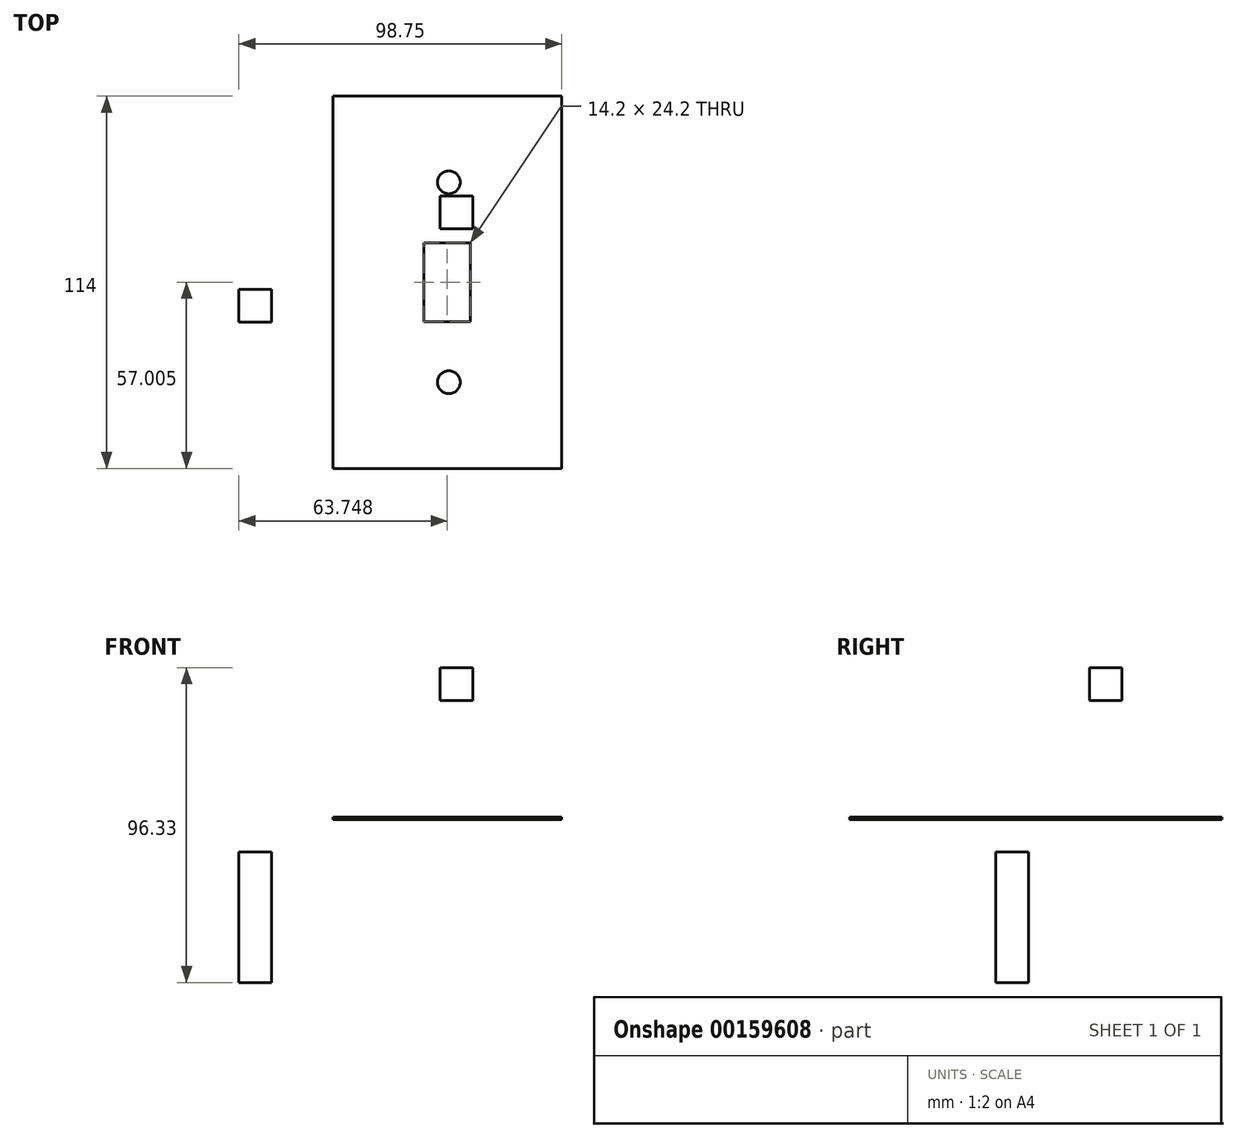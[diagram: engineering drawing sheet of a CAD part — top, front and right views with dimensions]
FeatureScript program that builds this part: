
annotation { "Feature Type Name" : "Feature", "Feature Type Description" : "" }
export const myFeature = defineFeature(function(context is Context, id is Id, definition is map)
    precondition{}
    {
        {
            assignVariable(context, id + "F0", {"name" : "W", "anyValue" : 1});
        }
        {
            var Q0;
            Q0=qCreatedBy(makeId("Top.planeOp"),FACE);
            var sketch = newSketch(context, id + "F1", { "sketchPlane" : qUnion([Q0])});
            skLineSegment(sketch, "E0.bottom", {"start": v(-32.81, 59.22) * mm, "end": v(37.19, 59.22) * mm});
            skLineSegment(sketch, "E0.top", {"start": v(-32.81, -54.78) * mm, "end": v(37.19, -54.78) * mm});
            skLineSegment(sketch, "E0.left", {"start": v(-32.81, 59.22) * mm, "end": v(-32.81, -54.78) * mm});
            skLineSegment(sketch, "E0.right", {"start": v(37.19, 59.22) * mm, "end": v(37.19, -54.78) * mm});
            skLineSegment(sketch, "E1.bottom", {"start": v(-4.91, 14.32) * mm, "end": v(9.29, 14.32) * mm});
            skLineSegment(sketch, "E1.top", {"start": v(-4.91, -9.88) * mm, "end": v(9.29, -9.88) * mm});
            skLineSegment(sketch, "E1.left", {"start": v(-4.91, 14.32) * mm, "end": v(-4.91, -9.88) * mm});
            skLineSegment(sketch, "E1.right", {"start": v(9.29, 14.32) * mm, "end": v(9.29, -9.88) * mm});
            skCircle(sketch, "E2", {"center": v(2.69, 32.82) * mm, "radius": 3.5 * mm});
            skCircle(sketch, "E3", {"center": v(2.69, -28.38) * mm, "radius": 3.5 * mm});
            skSolve(sketch);
        }
        {
            var Q0;
            Q0=makeQuery(id+"F1.imprint","IMPRINT",FACE,{"disambiguationData":[TD([[makeQuery(id+"F1.imprint","IMPRINT",EDGE,{"derivedFrom":sQuery(id+"F1.wireOp",EDGE,"E0.bottom")}),-1.0]])]});
            extrude(context, id + "F2", {"entities" : qUnion([Q0]), "depth" : (getVariable(context, 'W') * .671) * mm});
        }
        {
            var Q0;
            Q0=makeQuery(id+"F2.opExtrude","CAP_EDGE",EDGE,{"disambiguationData":[OSD([sQuery(id+"F1.wireOp",EDGE,"E2")])],"isStart":false});
            var Q1;
            Q1=makeQuery(id+"F2.opExtrude","CAP_EDGE",EDGE,{"disambiguationData":[OSD([sQuery(id+"F1.wireOp",EDGE,"E3")])],"isStart":false});
            fillet(context, id + "F3", {"entities" : qUnion([Q0, Q1]), "radius" : 1 * mm, "tangentPropagation" : true, "allowEdgeOverflow" : false});
        }
        {
            var Q0;
            Q0=qCreatedBy(makeId("Front.planeOp"),FACE);
            var sketch = newSketch(context, id + "F4", { "sketchPlane" : qUnion([Q0])});
            skLineSegment(sketch, "E4.bottom", {"start": v(-61.56, -9.89) * mm, "end": v(-51.56, -9.89) * mm});
            skLineSegment(sketch, "E4.top", {"start": v(-61.56, -49.89) * mm, "end": v(-51.56, -49.89) * mm});
            skLineSegment(sketch, "E4.left", {"start": v(-61.56, -9.89) * mm, "end": v(-61.56, -49.89) * mm});
            skLineSegment(sketch, "E4.right", {"start": v(-51.56, -9.89) * mm, "end": v(-51.56, -49.89) * mm});
            skSolve(sketch);
        }
        {
            var Q0;
            Q0=makeQuery(id+"F4.imprint","IMPRINT",FACE,{"disambiguationData":[TD([[makeQuery(id+"F4.imprint","IMPRINT",EDGE,{"derivedFrom":sQuery(id+"F4.wireOp",EDGE,"E4.bottom")}),-1.0]])]});
            extrude(context, id + "F5", {"entities" : qUnion([Q0]), "depth" : 10 * mm});
        }
        {
            var Q0;
            Q0=qCreatedBy(makeId("Right.planeOp"),FACE);
            var sketch = newSketch(context, id + "F6", { "sketchPlane" : qUnion([Q0])});
            skLineSegment(sketch, "E5.bottom", {"start": v(28.63, 46.44) * mm, "end": v(18.63, 46.44) * mm});
            skLineSegment(sketch, "E5.top", {"start": v(28.63, 36.44) * mm, "end": v(18.63, 36.44) * mm});
            skLineSegment(sketch, "E5.left", {"start": v(28.63, 46.44) * mm, "end": v(28.63, 36.44) * mm});
            skLineSegment(sketch, "E5.right", {"start": v(18.63, 46.44) * mm, "end": v(18.63, 36.44) * mm});
            skSolve(sketch);
        }
        {
            var Q0;
            Q0=makeQuery(id+"F6.imprint","IMPRINT",FACE,{"disambiguationData":[TD([[makeQuery(id+"F6.imprint","IMPRINT",EDGE,{"derivedFrom":sQuery(id+"F6.wireOp",EDGE,"E5.bottom")}),1.0]])]});
            extrude(context, id + "F7", {"entities" : qUnion([Q0]), "depth" : 10 * mm});
        }
    });
